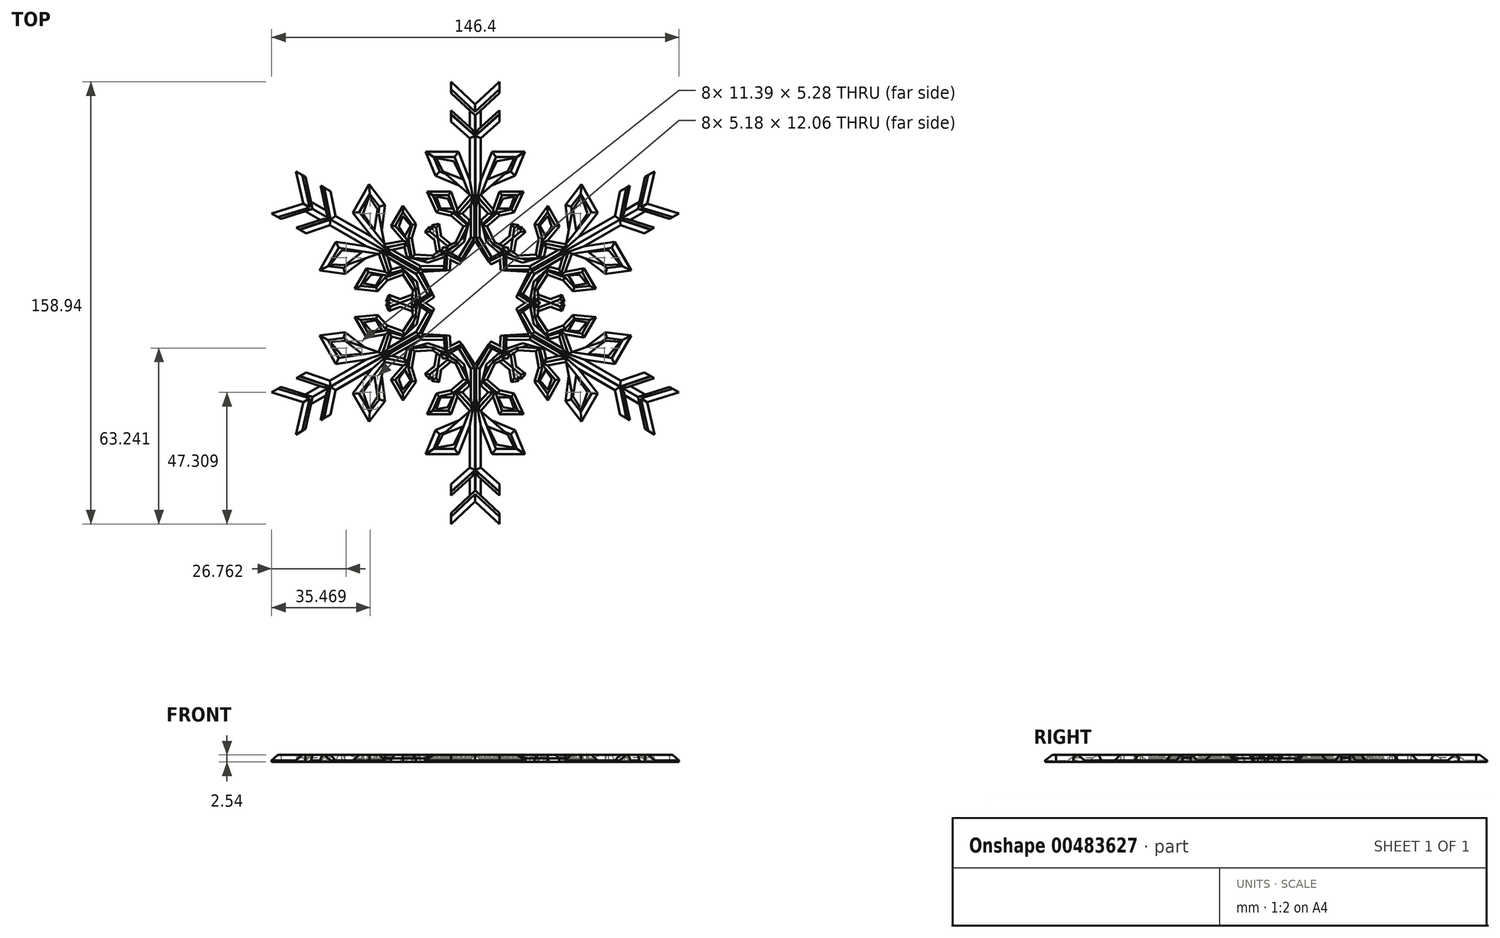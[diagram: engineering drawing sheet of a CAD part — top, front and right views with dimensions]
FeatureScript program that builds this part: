
annotation { "Feature Type Name" : "Feature", "Feature Type Description" : "" }
export const myFeature = defineFeature(function(context is Context, id is Id, definition is map)
    precondition{}
    {
        {
            var Q0;
            Q0=qCreatedBy(makeId("Top.planeOp"),FACE);
            var sketch = newSketch(context, id + "F0", { "sketchPlane" : qUnion([Q0])});
            skLineSegment(sketch, "E0", {"start": v(0, 65) * mm, "end": v(-8.74, 73.12) * mm});
            skLineSegment(sketch, "E1", {"start": v(-8.74, 73.12) * mm, "end": v(-8.74, 69.16) * mm});
            skLineSegment(sketch, "E2", {"start": v(-8.74, 69.16) * mm, "end": v(-1.96, 62.92) * mm});
            skLineSegment(sketch, "E3", {"start": v(-1.96, 62.92) * mm, "end": v(-1.96, 56.82) * mm});
            skLineSegment(sketch, "E4", {"start": v(-1.96, 56.82) * mm, "end": v(-8.74, 62.92) * mm});
            skLineSegment(sketch, "E5", {"start": v(-8.74, 62.92) * mm, "end": v(-8.74, 58.8) * mm});
            skLineSegment(sketch, "E6", {"start": v(-8.74, 58.8) * mm, "end": v(-1.96, 52.84) * mm});
            skLineSegment(sketch, "E7", {"start": v(-1.96, 52.84) * mm, "end": v(-1.96, 37.67) * mm});
            skLineSegment(sketch, "E8", {"start": v(-1.96, 37.67) * mm, "end": v(-6.07, 48.02) * mm});
            skLineSegment(sketch, "E9", {"start": v(-6.07, 48.02) * mm, "end": v(-17.85, 48.02) * mm});
            skLineSegment(sketch, "E10", {"start": v(-17.85, 48.02) * mm, "end": v(-14.3, 39.37) * mm});
            skLineSegment(sketch, "E11", {"start": v(-14.3, 39.37) * mm, "end": v(-5.8, 35.82) * mm});
            skLineSegment(sketch, "E12", {"start": v(-5.8, 35.82) * mm, "end": v(-1.96, 32.56) * mm});
            skLineSegment(sketch, "E13", {"start": v(-1.96, 32.56) * mm, "end": v(-6.45, 27.29) * mm});
            skLineSegment(sketch, "E14", {"start": v(-6.45, 27.29) * mm, "end": v(-8.74, 33.7) * mm});
            skLineSegment(sketch, "E15", {"start": v(-8.74, 33.7) * mm, "end": v(-17.28, 33.7) * mm});
            skLineSegment(sketch, "E16", {"start": v(-17.28, 33.7) * mm, "end": v(-13.88, 26.18) * mm});
            skLineSegment(sketch, "E17", {"start": v(-13.88, 26.18) * mm, "end": v(-8.74, 25.04) * mm});
            skLineSegment(sketch, "E18", {"start": v(-8.74, 25.04) * mm, "end": v(-4.2, 21.18) * mm});
            skLineSegment(sketch, "E19", {"start": v(-4.2, 21.18) * mm, "end": v(-7.07, 15.4) * mm});
            skLineSegment(sketch, "E20", {"start": v(-7.07, 15.4) * mm, "end": v(-11.6, 13.4) * mm});
            skLineSegment(sketch, "E21", {"start": v(-11.6, 13.4) * mm, "end": v(-13.03, 22.06) * mm});
            skLineSegment(sketch, "E22", {"start": v(-13.03, 22.06) * mm, "end": v(-15.53, 21.65) * mm});
            skLineSegment(sketch, "E23", {"start": v(-15.53, 21.65) * mm, "end": v(-13.9, 11.7) * mm});
            skLineSegment(sketch, "E24", {"start": v(-13.9, 11.7) * mm, "end": v(-5.65, 7.45) * mm});
            skLineSegment(sketch, "E25", {"start": v(-5.65, 7.45) * mm, "end": v(0, 15.96) * mm});
            skLineSegment(sketch, "E26", {"start": v(0, 15.96) * mm, "end": v(0, 65) * mm});
            skSolve(sketch);
        }
        {
            var Q0;
            Q0=qCreatedBy(makeId("Top.planeOp"),FACE);
            var sketch = newSketch(context, id + "F1", { "sketchPlane" : qUnion([Q0])});
            skLineSegment(sketch, "E27", {"start": v(-14.02, 45.75) * mm, "end": v(-11.6, 40.93) * mm});
            skLineSegment(sketch, "E28", {"start": v(-11.6, 40.93) * mm, "end": v(-4.51, 38.1) * mm});
            skLineSegment(sketch, "E29", {"start": v(-4.51, 38.1) * mm, "end": v(-7.64, 44.62) * mm});
            skLineSegment(sketch, "E30", {"start": v(-7.64, 44.62) * mm, "end": v(-14.02, 45.75) * mm});
            skLineSegment(sketch, "E31", {"start": v(-14.02, 31.85) * mm, "end": v(-12.46, 27.6) * mm});
            skLineSegment(sketch, "E32", {"start": v(-12.46, 27.6) * mm, "end": v(-8.2, 27.6) * mm});
            skLineSegment(sketch, "E33", {"start": v(-8.2, 27.6) * mm, "end": v(-9.9, 31.14) * mm});
            skLineSegment(sketch, "E34", {"start": v(-9.9, 31.14) * mm, "end": v(-14.02, 31.85) * mm});
            skLineSegment(sketch, "E35", {"start": v(-1.54, 29.01) * mm, "end": v(-4.66, 25.75) * mm});
            skLineSegment(sketch, "E36", {"start": v(-4.66, 25.75) * mm, "end": v(-2.12, 23.33) * mm});
            skLineSegment(sketch, "E37", {"start": v(-2.12, 23.33) * mm, "end": v(-3.95, 15.68) * mm});
            skLineSegment(sketch, "E38", {"start": v(-3.95, 15.68) * mm, "end": v(-8.77, 11.42) * mm});
            skLineSegment(sketch, "E39", {"start": v(-8.77, 11.42) * mm, "end": v(-5.93, 10) * mm});
            skLineSegment(sketch, "E40", {"start": v(-5.93, 10) * mm, "end": v(-1.63, 17.21) * mm});
            skLineSegment(sketch, "E41", {"start": v(-1.54, 29.01) * mm, "end": v(-1.63, 17.21) * mm});
            skSolve(sketch);
        }
        {
            var Q0;
            Q0=qCreatedBy(makeId("Top.planeOp"),FACE);
            var sketch = newSketch(context, id + "F2", { "sketchPlane" : qUnion([Q0])});
            skCircle(sketch, "E42", {"center": v(0, 0) * mm, "radius": 4.51 * mm});
            skSolve(sketch);
        }
        {
            var Q0;
            Q0 = qSketchRegion(id + "F0", true);
            extrude(context, id + "F3", {"entities" : qUnion([Q0]), "depth" : 2.54 * mm});
        }
        {
            var Q0;
            Q0 = qSketchRegion(id + "F1", true);
            extrude(context, id + "F4", {"entities" : qUnion([Q0]), "operationType" : NewBodyOperationType.REMOVE, "endBound" : BoundingType.THROUGH_ALL, "oppositeDirection" : true, "depth" : 25.4 * mm, "hasSecondDirection" : true, "secondDirectionOppositeDirection" : false, "secondDirectionDepth" : 25.4 * mm});
        }
        {
            var Q0;
            Q0=makeQuery(id+"F6.opPattern","COPY",EDGE,{"derivedFrom":makeQuery(id+"F3.opExtrude","CAP_EDGE",EDGE,{"disambiguationData":[OSD([sQuery(id+"F0.wireOp",EDGE,"E7")])],"isStart":false}),"instanceName":"1"});
            var Q1;
            Q1=makeQuery(id+"F3.opExtrude","CAP_EDGE",EDGE,{"disambiguationData":[OSD([sQuery(id+"F0.wireOp",EDGE,"E7")])],"isStart":false});
            var Q2;
            Q2=makeQuery(id+"F3.opExtrude","CAP_EDGE",EDGE,{"disambiguationData":[OSD([sQuery(id+"F0.wireOp",EDGE,"E3")])],"isStart":false});
            var Q3;
            Q3=makeQuery(id+"F6.opPattern","COPY",EDGE,{"derivedFrom":makeQuery(id+"F3.opExtrude","CAP_EDGE",EDGE,{"disambiguationData":[OSD([sQuery(id+"F0.wireOp",EDGE,"E3")])],"isStart":false}),"instanceName":"1"});
            var Q4;
            Q4=makeQuery(id+"F3.opExtrude","CAP_EDGE",EDGE,{"disambiguationData":[OSD([sQuery(id+"F0.wireOp",EDGE,"E8")])],"isStart":false});
            var Q5;
            Q5=makeQuery(id+"F3.opExtrude","CAP_EDGE",EDGE,{"disambiguationData":[OSD([sQuery(id+"F0.wireOp",EDGE,"E9")])],"isStart":false});
            var Q6;
            Q6=makeQuery(id+"F3.opExtrude","CAP_EDGE",EDGE,{"disambiguationData":[OSD([sQuery(id+"F0.wireOp",EDGE,"E10")])],"isStart":false});
            var Q7;
            Q7=makeQuery(id+"F3.opExtrude","CAP_EDGE",EDGE,{"disambiguationData":[OSD([sQuery(id+"F0.wireOp",EDGE,"E11")])],"isStart":false});
            var Q8;
            Q8=makeQuery(id+"F3.opExtrude","CAP_EDGE",EDGE,{"disambiguationData":[OSD([sQuery(id+"F0.wireOp",EDGE,"E6")])],"isStart":false});
            var Q9;
            Q9=makeQuery(id+"F3.opExtrude","CAP_EDGE",EDGE,{"disambiguationData":[OSD([sQuery(id+"F0.wireOp",EDGE,"E0")])],"isStart":false});
            chamfer(context, id + "F5", {"entities" : qUnion([Q0, Q1, Q2, Q3, Q4, Q5, Q6, Q7, Q8, Q9]), "width" : 1.96 * mm, "tangentPropagation" : true});
        }
        {
            var Q0;
            Q0=makeQuery(id+"F3.opExtrude","SWEPT_BODY",BODY,{"disambiguationData":[OSD([sQuery(id+"F0.wireOp",EDGE,"E0"),sQuery(id+"F0.wireOp",EDGE,"E1"),sQuery(id+"F0.wireOp",EDGE,"E2"),sQuery(id+"F0.wireOp",EDGE,"E3"),sQuery(id+"F0.wireOp",EDGE,"E4"),sQuery(id+"F0.wireOp",EDGE,"E5"),sQuery(id+"F0.wireOp",EDGE,"E6"),sQuery(id+"F0.wireOp",EDGE,"E7"),sQuery(id+"F0.wireOp",EDGE,"E8"),sQuery(id+"F0.wireOp",EDGE,"E9"),sQuery(id+"F0.wireOp",EDGE,"E10"),sQuery(id+"F0.wireOp",EDGE,"E11"),sQuery(id+"F0.wireOp",EDGE,"E12"),sQuery(id+"F0.wireOp",EDGE,"E13"),sQuery(id+"F0.wireOp",EDGE,"E14"),sQuery(id+"F0.wireOp",EDGE,"E15"),sQuery(id+"F0.wireOp",EDGE,"E16"),sQuery(id+"F0.wireOp",EDGE,"E17"),sQuery(id+"F0.wireOp",EDGE,"E18"),sQuery(id+"F0.wireOp",EDGE,"E19"),sQuery(id+"F0.wireOp",EDGE,"E20"),sQuery(id+"F0.wireOp",EDGE,"E21"),sQuery(id+"F0.wireOp",EDGE,"E22"),sQuery(id+"F0.wireOp",EDGE,"E23"),sQuery(id+"F0.wireOp",EDGE,"E24"),sQuery(id+"F0.wireOp",EDGE,"E25"),sQuery(id+"F0.wireOp",EDGE,"E26")])]});
            var Q1;
            Q1=qCreatedBy(makeId("Right.planeOp"),FACE);
            mirror(context, id + "F6", {"operationType" : NewBodyOperationType.ADD, "entities" : qUnion([Q0]), "mirrorPlane" : qUnion([Q1])});
        }
        {
            var Q0;
            Q0=makeQuery(id+"F3.opExtrude","CAP_EDGE",EDGE,{"disambiguationData":[OSD([sQuery(id+"F0.wireOp",EDGE,"E15")])],"isStart":false});
            var Q1;
            Q1=makeQuery(id+"F3.opExtrude","CAP_EDGE",EDGE,{"disambiguationData":[OSD([sQuery(id+"F0.wireOp",EDGE,"E16")])],"isStart":false});
            var Q2;
            Q2=makeQuery(id+"F3.opExtrude","CAP_EDGE",EDGE,{"disambiguationData":[OSD([sQuery(id+"F0.wireOp",EDGE,"E17")])],"isStart":false});
            var Q3;
            Q3=makeQuery(id+"F3.opExtrude","CAP_EDGE",EDGE,{"disambiguationData":[OSD([sQuery(id+"F0.wireOp",EDGE,"E14")])],"isStart":false});
            var Q4;
            Q4=makeQuery(id+"F3.opExtrude","CAP_EDGE",EDGE,{"disambiguationData":[OSD([sQuery(id+"F0.wireOp",EDGE,"E18")])],"isStart":false});
            var Q5;
            Q5=makeQuery(id+"F3.opExtrude","CAP_EDGE",EDGE,{"disambiguationData":[OSD([sQuery(id+"F0.wireOp",EDGE,"E13")])],"isStart":false});
            var Q6;
            Q6=makeQuery(id+"F6.opPattern","COPY",EDGE,{"derivedFrom":makeQuery(id+"F3.opExtrude","CAP_EDGE",EDGE,{"disambiguationData":[OSD([sQuery(id+"F0.wireOp",EDGE,"E13")])],"isStart":false}),"instanceName":"1"});
            var Q7;
            Q7=makeQuery(id+"F6.opPattern","COPY",EDGE,{"derivedFrom":makeQuery(id+"F3.opExtrude","CAP_EDGE",EDGE,{"disambiguationData":[OSD([sQuery(id+"F0.wireOp",EDGE,"E14")])],"isStart":false}),"instanceName":"1"});
            var Q8;
            Q8=makeQuery(id+"F6.opPattern","COPY",EDGE,{"derivedFrom":makeQuery(id+"F3.opExtrude","CAP_EDGE",EDGE,{"disambiguationData":[OSD([sQuery(id+"F0.wireOp",EDGE,"E15")])],"isStart":false}),"instanceName":"1"});
            var Q9;
            Q9=makeQuery(id+"F6.opPattern","COPY",EDGE,{"derivedFrom":makeQuery(id+"F3.opExtrude","CAP_EDGE",EDGE,{"disambiguationData":[OSD([sQuery(id+"F0.wireOp",EDGE,"E16")])],"isStart":false}),"instanceName":"1"});
            var Q10;
            Q10=makeQuery(id+"F6.opPattern","COPY",EDGE,{"derivedFrom":makeQuery(id+"F3.opExtrude","CAP_EDGE",EDGE,{"disambiguationData":[OSD([sQuery(id+"F0.wireOp",EDGE,"E17")])],"isStart":false}),"instanceName":"1"});
            var Q11;
            Q11=makeQuery(id+"F6.opPattern","COPY",EDGE,{"derivedFrom":makeQuery(id+"F3.opExtrude","CAP_EDGE",EDGE,{"disambiguationData":[OSD([sQuery(id+"F0.wireOp",EDGE,"E18")])],"isStart":false}),"instanceName":"1"});
            var Q12;
            Q12=makeQuery(id+"F6.opPattern","COPY",EDGE,{"derivedFrom":makeQuery(id+"F4.boolean.opBoolean","INTERSECT",EDGE,{"derivedFrom":[makeQuery(id+"F3.opExtrude","CAP_FACE",FACE,{"disambiguationData":[OSD([sQuery(id+"F0.wireOp",EDGE,"E0"),sQuery(id+"F0.wireOp",EDGE,"E1"),sQuery(id+"F0.wireOp",EDGE,"E2"),sQuery(id+"F0.wireOp",EDGE,"E3"),sQuery(id+"F0.wireOp",EDGE,"E4"),sQuery(id+"F0.wireOp",EDGE,"E5"),sQuery(id+"F0.wireOp",EDGE,"E6"),sQuery(id+"F0.wireOp",EDGE,"E7"),sQuery(id+"F0.wireOp",EDGE,"E8"),sQuery(id+"F0.wireOp",EDGE,"E9"),sQuery(id+"F0.wireOp",EDGE,"E10"),sQuery(id+"F0.wireOp",EDGE,"E11"),sQuery(id+"F0.wireOp",EDGE,"E12"),sQuery(id+"F0.wireOp",EDGE,"E13"),sQuery(id+"F0.wireOp",EDGE,"E14"),sQuery(id+"F0.wireOp",EDGE,"E15"),sQuery(id+"F0.wireOp",EDGE,"E16"),sQuery(id+"F0.wireOp",EDGE,"E17"),sQuery(id+"F0.wireOp",EDGE,"E18"),sQuery(id+"F0.wireOp",EDGE,"E19"),sQuery(id+"F0.wireOp",EDGE,"E20"),sQuery(id+"F0.wireOp",EDGE,"E21"),sQuery(id+"F0.wireOp",EDGE,"E22"),sQuery(id+"F0.wireOp",EDGE,"E23"),sQuery(id+"F0.wireOp",EDGE,"E24"),sQuery(id+"F0.wireOp",EDGE,"E25"),sQuery(id+"F0.wireOp",EDGE,"E26")])],"isStart":false}),makeQuery(id+"F4.opExtrude","SWEPT_FACE",FACE,{"disambiguationData":[OSD([sQuery(id+"F1.wireOp",EDGE,"E41")])]})]}),"instanceName":"1"});
            var Q13;
            Q13=makeQuery(id+"F4.boolean.opBoolean","INTERSECT",EDGE,{"derivedFrom":[makeQuery(id+"F3.opExtrude","CAP_FACE",FACE,{"disambiguationData":[OSD([sQuery(id+"F0.wireOp",EDGE,"E0"),sQuery(id+"F0.wireOp",EDGE,"E1"),sQuery(id+"F0.wireOp",EDGE,"E2"),sQuery(id+"F0.wireOp",EDGE,"E3"),sQuery(id+"F0.wireOp",EDGE,"E4"),sQuery(id+"F0.wireOp",EDGE,"E5"),sQuery(id+"F0.wireOp",EDGE,"E6"),sQuery(id+"F0.wireOp",EDGE,"E7"),sQuery(id+"F0.wireOp",EDGE,"E8"),sQuery(id+"F0.wireOp",EDGE,"E9"),sQuery(id+"F0.wireOp",EDGE,"E10"),sQuery(id+"F0.wireOp",EDGE,"E11"),sQuery(id+"F0.wireOp",EDGE,"E12"),sQuery(id+"F0.wireOp",EDGE,"E13"),sQuery(id+"F0.wireOp",EDGE,"E14"),sQuery(id+"F0.wireOp",EDGE,"E15"),sQuery(id+"F0.wireOp",EDGE,"E16"),sQuery(id+"F0.wireOp",EDGE,"E17"),sQuery(id+"F0.wireOp",EDGE,"E18"),sQuery(id+"F0.wireOp",EDGE,"E19"),sQuery(id+"F0.wireOp",EDGE,"E20"),sQuery(id+"F0.wireOp",EDGE,"E21"),sQuery(id+"F0.wireOp",EDGE,"E22"),sQuery(id+"F0.wireOp",EDGE,"E23"),sQuery(id+"F0.wireOp",EDGE,"E24"),sQuery(id+"F0.wireOp",EDGE,"E25"),sQuery(id+"F0.wireOp",EDGE,"E26")])],"isStart":false}),makeQuery(id+"F4.opExtrude","SWEPT_FACE",FACE,{"disambiguationData":[OSD([sQuery(id+"F1.wireOp",EDGE,"E41")])]})]});
            chamfer(context, id + "F7", {"entities" : qUnion([Q0, Q1, Q2, Q3, Q4, Q5, Q6, Q7, Q8, Q9, Q10, Q11, Q12, Q13]), "width" : 1.27 * mm, "tangentPropagation" : true});
        }
        {
            var Q0;
            Q0=makeQuery(id+"F3.opExtrude","CAP_EDGE",EDGE,{"disambiguationData":[OSD([sQuery(id+"F0.wireOp",EDGE,"E22")])],"isStart":false});
            var Q1;
            Q1=makeQuery(id+"F6.opPattern","COPY",EDGE,{"derivedFrom":makeQuery(id+"F3.opExtrude","CAP_EDGE",EDGE,{"disambiguationData":[OSD([sQuery(id+"F0.wireOp",EDGE,"E22")])],"isStart":false}),"instanceName":"1"});
            var Q2;
            Q2=makeQuery(id+"F3.opExtrude","CAP_EDGE",EDGE,{"disambiguationData":[OSD([sQuery(id+"F0.wireOp",EDGE,"E23")])],"isStart":false});
            var Q3;
            Q3=makeQuery(id+"F3.opExtrude","CAP_EDGE",EDGE,{"disambiguationData":[OSD([sQuery(id+"F0.wireOp",EDGE,"E21")])],"isStart":false});
            var Q4;
            Q4=makeQuery(id+"F6.opPattern","COPY",EDGE,{"derivedFrom":makeQuery(id+"F3.opExtrude","CAP_EDGE",EDGE,{"disambiguationData":[OSD([sQuery(id+"F0.wireOp",EDGE,"E21")])],"isStart":false}),"instanceName":"1"});
            var Q5;
            Q5=makeQuery(id+"F6.opPattern","COPY",EDGE,{"derivedFrom":makeQuery(id+"F3.opExtrude","CAP_EDGE",EDGE,{"disambiguationData":[OSD([sQuery(id+"F0.wireOp",EDGE,"E23")])],"isStart":false}),"instanceName":"1"});
            var Q6;
            Q6=makeQuery(id+"F3.opExtrude","CAP_EDGE",EDGE,{"disambiguationData":[OSD([sQuery(id+"F0.wireOp",EDGE,"E19")])],"isStart":false});
            var Q7;
            Q7=makeQuery(id+"F3.opExtrude","CAP_EDGE",EDGE,{"disambiguationData":[OSD([sQuery(id+"F0.wireOp",EDGE,"E20")])],"isStart":false});
            var Q8;
            Q8=makeQuery(id+"F6.opPattern","COPY",EDGE,{"derivedFrom":makeQuery(id+"F3.opExtrude","CAP_EDGE",EDGE,{"disambiguationData":[OSD([sQuery(id+"F0.wireOp",EDGE,"E20")])],"isStart":false}),"instanceName":"1"});
            var Q9;
            Q9=makeQuery(id+"F6.opPattern","COPY",EDGE,{"derivedFrom":makeQuery(id+"F3.opExtrude","CAP_EDGE",EDGE,{"disambiguationData":[OSD([sQuery(id+"F0.wireOp",EDGE,"E19")])],"isStart":false}),"instanceName":"1"});
            var Q10;
            Q10=makeQuery(id+"F6.opPattern","COPY",EDGE,{"derivedFrom":makeQuery(id+"F4.boolean.opBoolean","INTERSECT",EDGE,{"derivedFrom":[makeQuery(id+"F3.opExtrude","CAP_FACE",FACE,{"disambiguationData":[OSD([sQuery(id+"F0.wireOp",EDGE,"E0"),sQuery(id+"F0.wireOp",EDGE,"E1"),sQuery(id+"F0.wireOp",EDGE,"E2"),sQuery(id+"F0.wireOp",EDGE,"E3"),sQuery(id+"F0.wireOp",EDGE,"E4"),sQuery(id+"F0.wireOp",EDGE,"E5"),sQuery(id+"F0.wireOp",EDGE,"E6"),sQuery(id+"F0.wireOp",EDGE,"E7"),sQuery(id+"F0.wireOp",EDGE,"E8"),sQuery(id+"F0.wireOp",EDGE,"E9"),sQuery(id+"F0.wireOp",EDGE,"E10"),sQuery(id+"F0.wireOp",EDGE,"E11"),sQuery(id+"F0.wireOp",EDGE,"E12"),sQuery(id+"F0.wireOp",EDGE,"E13"),sQuery(id+"F0.wireOp",EDGE,"E14"),sQuery(id+"F0.wireOp",EDGE,"E15"),sQuery(id+"F0.wireOp",EDGE,"E16"),sQuery(id+"F0.wireOp",EDGE,"E17"),sQuery(id+"F0.wireOp",EDGE,"E18"),sQuery(id+"F0.wireOp",EDGE,"E19"),sQuery(id+"F0.wireOp",EDGE,"E20"),sQuery(id+"F0.wireOp",EDGE,"E21"),sQuery(id+"F0.wireOp",EDGE,"E22"),sQuery(id+"F0.wireOp",EDGE,"E23"),sQuery(id+"F0.wireOp",EDGE,"E24"),sQuery(id+"F0.wireOp",EDGE,"E25"),sQuery(id+"F0.wireOp",EDGE,"E26")])],"isStart":false}),makeQuery(id+"F4.opExtrude","SWEPT_FACE",FACE,{"disambiguationData":[OSD([sQuery(id+"F1.wireOp",EDGE,"E40")])]})]}),"instanceName":"1"});
            var Q11;
            Q11=makeQuery(id+"F4.boolean.opBoolean","INTERSECT",EDGE,{"derivedFrom":[makeQuery(id+"F3.opExtrude","CAP_FACE",FACE,{"disambiguationData":[OSD([sQuery(id+"F0.wireOp",EDGE,"E0"),sQuery(id+"F0.wireOp",EDGE,"E1"),sQuery(id+"F0.wireOp",EDGE,"E2"),sQuery(id+"F0.wireOp",EDGE,"E3"),sQuery(id+"F0.wireOp",EDGE,"E4"),sQuery(id+"F0.wireOp",EDGE,"E5"),sQuery(id+"F0.wireOp",EDGE,"E6"),sQuery(id+"F0.wireOp",EDGE,"E7"),sQuery(id+"F0.wireOp",EDGE,"E8"),sQuery(id+"F0.wireOp",EDGE,"E9"),sQuery(id+"F0.wireOp",EDGE,"E10"),sQuery(id+"F0.wireOp",EDGE,"E11"),sQuery(id+"F0.wireOp",EDGE,"E12"),sQuery(id+"F0.wireOp",EDGE,"E13"),sQuery(id+"F0.wireOp",EDGE,"E14"),sQuery(id+"F0.wireOp",EDGE,"E15"),sQuery(id+"F0.wireOp",EDGE,"E16"),sQuery(id+"F0.wireOp",EDGE,"E17"),sQuery(id+"F0.wireOp",EDGE,"E18"),sQuery(id+"F0.wireOp",EDGE,"E19"),sQuery(id+"F0.wireOp",EDGE,"E20"),sQuery(id+"F0.wireOp",EDGE,"E21"),sQuery(id+"F0.wireOp",EDGE,"E22"),sQuery(id+"F0.wireOp",EDGE,"E23"),sQuery(id+"F0.wireOp",EDGE,"E24"),sQuery(id+"F0.wireOp",EDGE,"E25"),sQuery(id+"F0.wireOp",EDGE,"E26")])],"isStart":false}),makeQuery(id+"F4.opExtrude","SWEPT_FACE",FACE,{"disambiguationData":[OSD([sQuery(id+"F1.wireOp",EDGE,"E40")])]})]});
            var Q12;
            Q12=makeQuery(id+"F6.opPattern","COPY",EDGE,{"derivedFrom":makeQuery(id+"F3.opExtrude","CAP_EDGE",EDGE,{"disambiguationData":[OSD([sQuery(id+"F0.wireOp",EDGE,"E24")])],"isStart":false}),"instanceName":"1"});
            var Q13;
            Q13=makeQuery(id+"F3.opExtrude","CAP_EDGE",EDGE,{"disambiguationData":[OSD([sQuery(id+"F0.wireOp",EDGE,"E24")])],"isStart":false});
            var Q14;
            Q14=makeQuery(id+"F6.opPattern","COPY",EDGE,{"derivedFrom":makeQuery(id+"F4.boolean.opBoolean","INTERSECT",EDGE,{"derivedFrom":[makeQuery(id+"F3.opExtrude","CAP_FACE",FACE,{"disambiguationData":[OSD([sQuery(id+"F0.wireOp",EDGE,"E0"),sQuery(id+"F0.wireOp",EDGE,"E1"),sQuery(id+"F0.wireOp",EDGE,"E2"),sQuery(id+"F0.wireOp",EDGE,"E3"),sQuery(id+"F0.wireOp",EDGE,"E4"),sQuery(id+"F0.wireOp",EDGE,"E5"),sQuery(id+"F0.wireOp",EDGE,"E6"),sQuery(id+"F0.wireOp",EDGE,"E7"),sQuery(id+"F0.wireOp",EDGE,"E8"),sQuery(id+"F0.wireOp",EDGE,"E9"),sQuery(id+"F0.wireOp",EDGE,"E10"),sQuery(id+"F0.wireOp",EDGE,"E11"),sQuery(id+"F0.wireOp",EDGE,"E12"),sQuery(id+"F0.wireOp",EDGE,"E13"),sQuery(id+"F0.wireOp",EDGE,"E14"),sQuery(id+"F0.wireOp",EDGE,"E15"),sQuery(id+"F0.wireOp",EDGE,"E16"),sQuery(id+"F0.wireOp",EDGE,"E17"),sQuery(id+"F0.wireOp",EDGE,"E18"),sQuery(id+"F0.wireOp",EDGE,"E19"),sQuery(id+"F0.wireOp",EDGE,"E20"),sQuery(id+"F0.wireOp",EDGE,"E21"),sQuery(id+"F0.wireOp",EDGE,"E22"),sQuery(id+"F0.wireOp",EDGE,"E23"),sQuery(id+"F0.wireOp",EDGE,"E24"),sQuery(id+"F0.wireOp",EDGE,"E25"),sQuery(id+"F0.wireOp",EDGE,"E26")])],"isStart":false}),makeQuery(id+"F4.opExtrude","SWEPT_FACE",FACE,{"disambiguationData":[OSD([sQuery(id+"F1.wireOp",EDGE,"E36")])]})]}),"instanceName":"1"});
            var Q15;
            Q15=makeQuery(id+"F4.boolean.opBoolean","INTERSECT",EDGE,{"derivedFrom":[makeQuery(id+"F3.opExtrude","CAP_FACE",FACE,{"disambiguationData":[OSD([sQuery(id+"F0.wireOp",EDGE,"E0"),sQuery(id+"F0.wireOp",EDGE,"E1"),sQuery(id+"F0.wireOp",EDGE,"E2"),sQuery(id+"F0.wireOp",EDGE,"E3"),sQuery(id+"F0.wireOp",EDGE,"E4"),sQuery(id+"F0.wireOp",EDGE,"E5"),sQuery(id+"F0.wireOp",EDGE,"E6"),sQuery(id+"F0.wireOp",EDGE,"E7"),sQuery(id+"F0.wireOp",EDGE,"E8"),sQuery(id+"F0.wireOp",EDGE,"E9"),sQuery(id+"F0.wireOp",EDGE,"E10"),sQuery(id+"F0.wireOp",EDGE,"E11"),sQuery(id+"F0.wireOp",EDGE,"E12"),sQuery(id+"F0.wireOp",EDGE,"E13"),sQuery(id+"F0.wireOp",EDGE,"E14"),sQuery(id+"F0.wireOp",EDGE,"E15"),sQuery(id+"F0.wireOp",EDGE,"E16"),sQuery(id+"F0.wireOp",EDGE,"E17"),sQuery(id+"F0.wireOp",EDGE,"E18"),sQuery(id+"F0.wireOp",EDGE,"E19"),sQuery(id+"F0.wireOp",EDGE,"E20"),sQuery(id+"F0.wireOp",EDGE,"E21"),sQuery(id+"F0.wireOp",EDGE,"E22"),sQuery(id+"F0.wireOp",EDGE,"E23"),sQuery(id+"F0.wireOp",EDGE,"E24"),sQuery(id+"F0.wireOp",EDGE,"E25"),sQuery(id+"F0.wireOp",EDGE,"E26")])],"isStart":false}),makeQuery(id+"F4.opExtrude","SWEPT_FACE",FACE,{"disambiguationData":[OSD([sQuery(id+"F1.wireOp",EDGE,"E36")])]})]});
            var Q16;
            Q16=makeQuery(id+"F4.boolean.opBoolean","INTERSECT",EDGE,{"derivedFrom":[makeQuery(id+"F3.opExtrude","CAP_FACE",FACE,{"disambiguationData":[OSD([sQuery(id+"F0.wireOp",EDGE,"E0"),sQuery(id+"F0.wireOp",EDGE,"E1"),sQuery(id+"F0.wireOp",EDGE,"E2"),sQuery(id+"F0.wireOp",EDGE,"E3"),sQuery(id+"F0.wireOp",EDGE,"E4"),sQuery(id+"F0.wireOp",EDGE,"E5"),sQuery(id+"F0.wireOp",EDGE,"E6"),sQuery(id+"F0.wireOp",EDGE,"E7"),sQuery(id+"F0.wireOp",EDGE,"E8"),sQuery(id+"F0.wireOp",EDGE,"E9"),sQuery(id+"F0.wireOp",EDGE,"E10"),sQuery(id+"F0.wireOp",EDGE,"E11"),sQuery(id+"F0.wireOp",EDGE,"E12"),sQuery(id+"F0.wireOp",EDGE,"E13"),sQuery(id+"F0.wireOp",EDGE,"E14"),sQuery(id+"F0.wireOp",EDGE,"E15"),sQuery(id+"F0.wireOp",EDGE,"E16"),sQuery(id+"F0.wireOp",EDGE,"E17"),sQuery(id+"F0.wireOp",EDGE,"E18"),sQuery(id+"F0.wireOp",EDGE,"E19"),sQuery(id+"F0.wireOp",EDGE,"E20"),sQuery(id+"F0.wireOp",EDGE,"E21"),sQuery(id+"F0.wireOp",EDGE,"E22"),sQuery(id+"F0.wireOp",EDGE,"E23"),sQuery(id+"F0.wireOp",EDGE,"E24"),sQuery(id+"F0.wireOp",EDGE,"E25"),sQuery(id+"F0.wireOp",EDGE,"E26")])],"isStart":false}),makeQuery(id+"F4.opExtrude","SWEPT_FACE",FACE,{"disambiguationData":[OSD([sQuery(id+"F1.wireOp",EDGE,"E35")])]})]});
            var Q17;
            Q17=makeQuery(id+"F6.opPattern","COPY",EDGE,{"derivedFrom":makeQuery(id+"F4.boolean.opBoolean","INTERSECT",EDGE,{"derivedFrom":[makeQuery(id+"F3.opExtrude","CAP_FACE",FACE,{"disambiguationData":[OSD([sQuery(id+"F0.wireOp",EDGE,"E0"),sQuery(id+"F0.wireOp",EDGE,"E1"),sQuery(id+"F0.wireOp",EDGE,"E2"),sQuery(id+"F0.wireOp",EDGE,"E3"),sQuery(id+"F0.wireOp",EDGE,"E4"),sQuery(id+"F0.wireOp",EDGE,"E5"),sQuery(id+"F0.wireOp",EDGE,"E6"),sQuery(id+"F0.wireOp",EDGE,"E7"),sQuery(id+"F0.wireOp",EDGE,"E8"),sQuery(id+"F0.wireOp",EDGE,"E9"),sQuery(id+"F0.wireOp",EDGE,"E10"),sQuery(id+"F0.wireOp",EDGE,"E11"),sQuery(id+"F0.wireOp",EDGE,"E12"),sQuery(id+"F0.wireOp",EDGE,"E13"),sQuery(id+"F0.wireOp",EDGE,"E14"),sQuery(id+"F0.wireOp",EDGE,"E15"),sQuery(id+"F0.wireOp",EDGE,"E16"),sQuery(id+"F0.wireOp",EDGE,"E17"),sQuery(id+"F0.wireOp",EDGE,"E18"),sQuery(id+"F0.wireOp",EDGE,"E19"),sQuery(id+"F0.wireOp",EDGE,"E20"),sQuery(id+"F0.wireOp",EDGE,"E21"),sQuery(id+"F0.wireOp",EDGE,"E22"),sQuery(id+"F0.wireOp",EDGE,"E23"),sQuery(id+"F0.wireOp",EDGE,"E24"),sQuery(id+"F0.wireOp",EDGE,"E25"),sQuery(id+"F0.wireOp",EDGE,"E26")])],"isStart":false}),makeQuery(id+"F4.opExtrude","SWEPT_FACE",FACE,{"disambiguationData":[OSD([sQuery(id+"F1.wireOp",EDGE,"E35")])]})]}),"instanceName":"1"});
            var Q18;
            Q18=makeQuery(id+"F6.opPattern","COPY",EDGE,{"derivedFrom":makeQuery(id+"F4.boolean.opBoolean","INTERSECT",EDGE,{"derivedFrom":[makeQuery(id+"F3.opExtrude","CAP_FACE",FACE,{"disambiguationData":[OSD([sQuery(id+"F0.wireOp",EDGE,"E0"),sQuery(id+"F0.wireOp",EDGE,"E1"),sQuery(id+"F0.wireOp",EDGE,"E2"),sQuery(id+"F0.wireOp",EDGE,"E3"),sQuery(id+"F0.wireOp",EDGE,"E4"),sQuery(id+"F0.wireOp",EDGE,"E5"),sQuery(id+"F0.wireOp",EDGE,"E6"),sQuery(id+"F0.wireOp",EDGE,"E7"),sQuery(id+"F0.wireOp",EDGE,"E8"),sQuery(id+"F0.wireOp",EDGE,"E9"),sQuery(id+"F0.wireOp",EDGE,"E10"),sQuery(id+"F0.wireOp",EDGE,"E11"),sQuery(id+"F0.wireOp",EDGE,"E12"),sQuery(id+"F0.wireOp",EDGE,"E13"),sQuery(id+"F0.wireOp",EDGE,"E14"),sQuery(id+"F0.wireOp",EDGE,"E15"),sQuery(id+"F0.wireOp",EDGE,"E16"),sQuery(id+"F0.wireOp",EDGE,"E17"),sQuery(id+"F0.wireOp",EDGE,"E18"),sQuery(id+"F0.wireOp",EDGE,"E19"),sQuery(id+"F0.wireOp",EDGE,"E20"),sQuery(id+"F0.wireOp",EDGE,"E21"),sQuery(id+"F0.wireOp",EDGE,"E22"),sQuery(id+"F0.wireOp",EDGE,"E23"),sQuery(id+"F0.wireOp",EDGE,"E24"),sQuery(id+"F0.wireOp",EDGE,"E25"),sQuery(id+"F0.wireOp",EDGE,"E26")])],"isStart":false}),makeQuery(id+"F4.opExtrude","SWEPT_FACE",FACE,{"disambiguationData":[OSD([sQuery(id+"F1.wireOp",EDGE,"E38")])]})]}),"instanceName":"1"});
            var Q19;
            Q19=makeQuery(id+"F4.boolean.opBoolean","INTERSECT",EDGE,{"derivedFrom":[makeQuery(id+"F3.opExtrude","CAP_FACE",FACE,{"disambiguationData":[OSD([sQuery(id+"F0.wireOp",EDGE,"E0"),sQuery(id+"F0.wireOp",EDGE,"E1"),sQuery(id+"F0.wireOp",EDGE,"E2"),sQuery(id+"F0.wireOp",EDGE,"E3"),sQuery(id+"F0.wireOp",EDGE,"E4"),sQuery(id+"F0.wireOp",EDGE,"E5"),sQuery(id+"F0.wireOp",EDGE,"E6"),sQuery(id+"F0.wireOp",EDGE,"E7"),sQuery(id+"F0.wireOp",EDGE,"E8"),sQuery(id+"F0.wireOp",EDGE,"E9"),sQuery(id+"F0.wireOp",EDGE,"E10"),sQuery(id+"F0.wireOp",EDGE,"E11"),sQuery(id+"F0.wireOp",EDGE,"E12"),sQuery(id+"F0.wireOp",EDGE,"E13"),sQuery(id+"F0.wireOp",EDGE,"E14"),sQuery(id+"F0.wireOp",EDGE,"E15"),sQuery(id+"F0.wireOp",EDGE,"E16"),sQuery(id+"F0.wireOp",EDGE,"E17"),sQuery(id+"F0.wireOp",EDGE,"E18"),sQuery(id+"F0.wireOp",EDGE,"E19"),sQuery(id+"F0.wireOp",EDGE,"E20"),sQuery(id+"F0.wireOp",EDGE,"E21"),sQuery(id+"F0.wireOp",EDGE,"E22"),sQuery(id+"F0.wireOp",EDGE,"E23"),sQuery(id+"F0.wireOp",EDGE,"E24"),sQuery(id+"F0.wireOp",EDGE,"E25"),sQuery(id+"F0.wireOp",EDGE,"E26")])],"isStart":false}),makeQuery(id+"F4.opExtrude","SWEPT_FACE",FACE,{"disambiguationData":[OSD([sQuery(id+"F1.wireOp",EDGE,"E38")])]})]});
            chamfer(context, id + "F8", {"entities" : qUnion([Q0, Q1, Q2, Q3, Q4, Q5, Q6, Q7, Q8, Q9, Q10, Q11, Q12, Q13, Q14, Q15, Q16, Q17, Q18, Q19]), "width" : 1.27 * mm, "tangentPropagation" : true});
        }
        {
            var Q0;
            Q0=makeQuery(id+"F3.opExtrude","CAP_EDGE",EDGE,{"disambiguationData":[OSD([sQuery(id+"F0.wireOp",EDGE,"E4")])],"isStart":false});
            var Q1;
            Q1=makeQuery(id+"F6.opPattern","COPY",EDGE,{"derivedFrom":makeQuery(id+"F3.opExtrude","CAP_EDGE",EDGE,{"disambiguationData":[OSD([sQuery(id+"F0.wireOp",EDGE,"E4")])],"isStart":false}),"instanceName":"1"});
            chamfer(context, id + "F9", {"entities" : qUnion([Q0, Q1]), "width" : 0.97 * mm, "tangentPropagation" : true});
        }
        {
            var Q0;
            Q0=qCreatedBy(makeId("Top.planeOp"),FACE);
            var sketch = newSketch(context, id + "F10", { "sketchPlane" : qUnion([Q0])});
            skCircle(sketch, "E43", {"center": v(0, 0) * mm, "radius": 5.14 * mm});
            skSolve(sketch);
        }
        {
            var Q0;
            Q0=makeQuery(id+"F3.opExtrude","SWEPT_BODY",BODY,{"disambiguationData":[OSD([sQuery(id+"F0.wireOp",EDGE,"E0"),sQuery(id+"F0.wireOp",EDGE,"E1"),sQuery(id+"F0.wireOp",EDGE,"E2"),sQuery(id+"F0.wireOp",EDGE,"E3"),sQuery(id+"F0.wireOp",EDGE,"E4"),sQuery(id+"F0.wireOp",EDGE,"E5"),sQuery(id+"F0.wireOp",EDGE,"E6"),sQuery(id+"F0.wireOp",EDGE,"E7"),sQuery(id+"F0.wireOp",EDGE,"E8"),sQuery(id+"F0.wireOp",EDGE,"E9"),sQuery(id+"F0.wireOp",EDGE,"E10"),sQuery(id+"F0.wireOp",EDGE,"E11"),sQuery(id+"F0.wireOp",EDGE,"E12"),sQuery(id+"F0.wireOp",EDGE,"E13"),sQuery(id+"F0.wireOp",EDGE,"E14"),sQuery(id+"F0.wireOp",EDGE,"E15"),sQuery(id+"F0.wireOp",EDGE,"E16"),sQuery(id+"F0.wireOp",EDGE,"E17"),sQuery(id+"F0.wireOp",EDGE,"E18"),sQuery(id+"F0.wireOp",EDGE,"E19"),sQuery(id+"F0.wireOp",EDGE,"E20"),sQuery(id+"F0.wireOp",EDGE,"E21"),sQuery(id+"F0.wireOp",EDGE,"E22"),sQuery(id+"F0.wireOp",EDGE,"E23"),sQuery(id+"F0.wireOp",EDGE,"E24"),sQuery(id+"F0.wireOp",EDGE,"E25"),sQuery(id+"F0.wireOp",EDGE,"E26")])]});
            var Q1;
            Q1=sQuery(id+"F2.wireOp",VERTEX,"E42.center");
            var Q2;
            {var subQ0=sQuery(id+"F0.wireOp",EDGE,"E0");var subQ1=makeQuery(id+"F5.opChamfer","BLEND_VERTEX",VERTEX,{"blendedFrom":[makeQuery(id+"F3.opExtrude","CAP_EDGE",EDGE,{"disambiguationData":[OSD([subQ0])],"isStart":false}),makeQuery(id+"F3.opExtrude","SWEPT_FACE",FACE,{"disambiguationData":[OSD([subQ0])]}),makeQuery(id+"F3.opExtrude","SWEPT_FACE",FACE,{"disambiguationData":[OSD([sQuery(id+"F0.wireOp",EDGE,"E26")])]})],"blendedInto":[makeQuery(id+"F3.opExtrude","SWEPT_FACE",FACE,{"disambiguationData":[OSD([subQ0])]}),makeQuery(id+"F3.opExtrude","SWEPT_FACE",FACE,{"disambiguationData":[OSD([sQuery(id+"F0.wireOp",EDGE,"E26")])]})]});Q2=makeQuery(id+"F6.boolean.opBoolean","MERGE",VERTEX,{"derivedFrom":[subQ1,makeQuery(id+"F6.opPattern","COPY",VERTEX,{"derivedFrom":subQ1,"instanceName":"1"})]});}
            var Q3;
            Q3=sQuery(id+"F2.wireOp",VERTEX,"E42.center");
            var Q4;
            {var subQ0=sQuery(id+"F0.wireOp",EDGE,"E0");var subQ1=makeQuery(id+"F5.opChamfer","BLEND_VERTEX",VERTEX,{"blendedFrom":[makeQuery(id+"F3.opExtrude","CAP_EDGE",EDGE,{"disambiguationData":[OSD([subQ0])],"isStart":false}),makeQuery(id+"F3.opExtrude","SWEPT_FACE",FACE,{"disambiguationData":[OSD([subQ0])]}),makeQuery(id+"F3.opExtrude","SWEPT_FACE",FACE,{"disambiguationData":[OSD([sQuery(id+"F0.wireOp",EDGE,"E26")])]})],"blendedInto":[makeQuery(id+"F3.opExtrude","SWEPT_FACE",FACE,{"disambiguationData":[OSD([subQ0])]}),makeQuery(id+"F3.opExtrude","SWEPT_FACE",FACE,{"disambiguationData":[OSD([sQuery(id+"F0.wireOp",EDGE,"E26")])]})]});Q4=makeQuery(id+"F6.boolean.opBoolean","MERGE",VERTEX,{"derivedFrom":[subQ1,makeQuery(id+"F6.opPattern","COPY",VERTEX,{"derivedFrom":subQ1,"instanceName":"1"})]});}
            transform(context, id + "F11", {"entities" : qUnion([Q0]), "transformType" : TransformType.TRANSLATION_DISTANCE, "transformDirection" : qUnion([Q3, Q4]), "distance" : 6.35 * mm, "makeCopy" : false});
        }
        {
            var Q0;
            Q0=makeQuery(id+"F3.opExtrude","SWEPT_BODY",BODY,{"disambiguationData":[OSD([sQuery(id+"F0.wireOp",EDGE,"E0"),sQuery(id+"F0.wireOp",EDGE,"E1"),sQuery(id+"F0.wireOp",EDGE,"E2"),sQuery(id+"F0.wireOp",EDGE,"E3"),sQuery(id+"F0.wireOp",EDGE,"E4"),sQuery(id+"F0.wireOp",EDGE,"E5"),sQuery(id+"F0.wireOp",EDGE,"E6"),sQuery(id+"F0.wireOp",EDGE,"E7"),sQuery(id+"F0.wireOp",EDGE,"E8"),sQuery(id+"F0.wireOp",EDGE,"E9"),sQuery(id+"F0.wireOp",EDGE,"E10"),sQuery(id+"F0.wireOp",EDGE,"E11"),sQuery(id+"F0.wireOp",EDGE,"E12"),sQuery(id+"F0.wireOp",EDGE,"E13"),sQuery(id+"F0.wireOp",EDGE,"E14"),sQuery(id+"F0.wireOp",EDGE,"E15"),sQuery(id+"F0.wireOp",EDGE,"E16"),sQuery(id+"F0.wireOp",EDGE,"E17"),sQuery(id+"F0.wireOp",EDGE,"E18"),sQuery(id+"F0.wireOp",EDGE,"E19"),sQuery(id+"F0.wireOp",EDGE,"E20"),sQuery(id+"F0.wireOp",EDGE,"E21"),sQuery(id+"F0.wireOp",EDGE,"E22"),sQuery(id+"F0.wireOp",EDGE,"E23"),sQuery(id+"F0.wireOp",EDGE,"E24"),sQuery(id+"F0.wireOp",EDGE,"E25"),sQuery(id+"F0.wireOp",EDGE,"E26")])]});
            var Q1;
            Q1=sQuery(id+"F10.wireOp",EDGE,"E43");
            circularPattern(context, id + "F12", {"entities" : qUnion([Q0]), "axis" : qUnion([Q1]), "angle" : 60 * degree, "instanceCount" : 6, "oppositeDirection" : true, "isCentered" : true, "computeTransformsWithoutBuiltin" : true});
        }
    });
